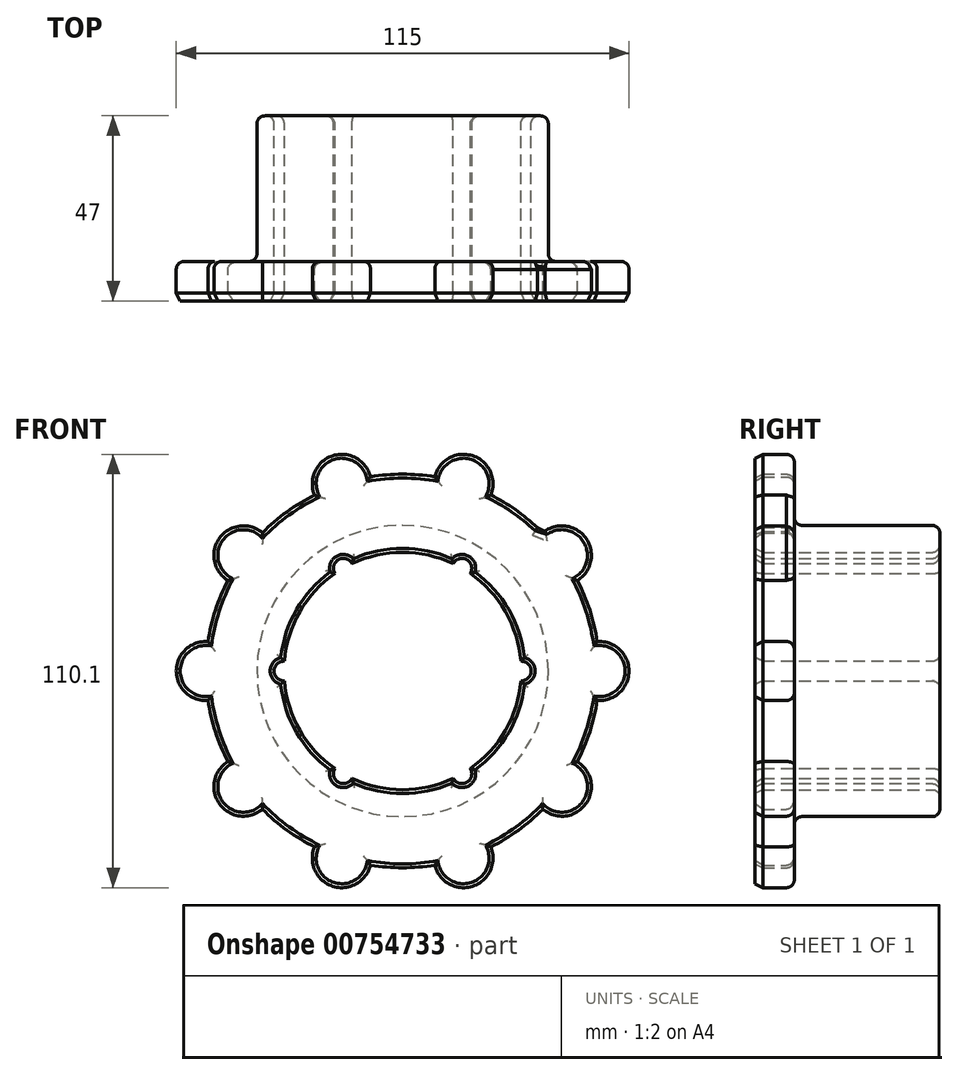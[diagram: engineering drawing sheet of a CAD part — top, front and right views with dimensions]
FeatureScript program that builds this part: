
annotation { "Feature Type Name" : "Feature", "Feature Type Description" : "" }
export const myFeature = defineFeature(function(context is Context, id is Id, definition is map)
    precondition{}
    {
        {
            var Q0;
            Q0=qCreatedBy(makeId("Front.planeOp"),FACE);
            var sketch = newSketch(context, id + "F0", { "sketchPlane" : qUnion([Q0])});
            skArc(sketch, "E0", {"start": v(30.05, 2.5) * mm, "mid": v(26.11, 15.07) * mm, "end": v(17.19, 24.77) * mm});
            skArc(sketch, "E1", {"start": v(30.05, -2.5) * mm, "mid": v(32.65, 0) * mm, "end": v(30.05, 2.5) * mm});
            skArc(sketch, "E2.1.0", {"start": v(17.19, 24.77) * mm, "mid": v(16.33, 28.28) * mm, "end": v(12.86, 27.27) * mm});
            skArc(sketch, "E2.2.0", {"start": v(-12.86, 27.27) * mm, "mid": v(-16.32, 28.28) * mm, "end": v(-17.19, 24.77) * mm});
            skArc(sketch, "E2.3.0", {"start": v(-30.05, 2.5) * mm, "mid": v(-32.65, 0) * mm, "end": v(-30.05, -2.5) * mm});
            skArc(sketch, "E2.4.0", {"start": v(-17.19, -24.77) * mm, "mid": v(-16.33, -28.28) * mm, "end": v(-12.86, -27.27) * mm});
            skArc(sketch, "E2.5.0", {"start": v(12.86, -27.27) * mm, "mid": v(16.33, -28.28) * mm, "end": v(17.19, -24.77) * mm});
            skArc(sketch, "E3.trimOffspring", {"start": v(-17.19, 24.77) * mm, "mid": v(-26.11, 15.08) * mm, "end": v(-30.05, 2.5) * mm});
            skArc(sketch, "E4.trimOffspring", {"start": v(-30.05, -2.5) * mm, "mid": v(-26.11, -15.07) * mm, "end": v(-17.19, -24.77) * mm});
            skArc(sketch, "E5.trimOffspring", {"start": v(-12.86, -27.27) * mm, "mid": v(0, -30.15) * mm, "end": v(12.86, -27.27) * mm});
            skArc(sketch, "E6.trimOffspring", {"start": v(17.19, -24.77) * mm, "mid": v(26.11, -15.07) * mm, "end": v(30.05, -2.5) * mm});
            skArc(sketch, "E7.trimOffspring", {"start": v(12.86, 27.27) * mm, "mid": v(0, 30.15) * mm, "end": v(-12.86, 27.27) * mm});
            skCircle(sketch, "E8", {"center": v(0, 0) * mm, "radius": 37 * mm});
            skSolve(sketch);
        }
        {
            var Q0;
            Q0=makeQuery(id+"F0.imprint","IMPRINT",FACE,{"disambiguationData":[TD([[makeQuery(id+"F0.imprint","IMPRINT",EDGE,{"derivedFrom":sQuery(id+"F0.wireOp",EDGE,"E0")}),-1.0]])]});
            extrude(context, id + "F1", {"entities" : qUnion([Q0]), "depth" : (24 + 13) * mm, "offsetDistance" : 25 * mm});
        }
        {
            var Q0;
            Q0=makeQuery(id+"F1.opExtrude","CAP_FACE",FACE,{"disambiguationData":[OSD([sQuery(id+"F0.wireOp",EDGE,"E0"),sQuery(id+"F0.wireOp",EDGE,"E1"),sQuery(id+"F0.wireOp",EDGE,"E2.1.0"),sQuery(id+"F0.wireOp",EDGE,"E2.2.0"),sQuery(id+"F0.wireOp",EDGE,"E2.3.0"),sQuery(id+"F0.wireOp",EDGE,"E2.4.0"),sQuery(id+"F0.wireOp",EDGE,"E2.5.0"),sQuery(id+"F0.wireOp",EDGE,"E3.trimOffspring"),sQuery(id+"F0.wireOp",EDGE,"E4.trimOffspring"),sQuery(id+"F0.wireOp",EDGE,"E5.trimOffspring"),sQuery(id+"F0.wireOp",EDGE,"E6.trimOffspring"),sQuery(id+"F0.wireOp",EDGE,"E7.trimOffspring"),sQuery(id+"F0.wireOp",EDGE,"E8")])],"isStart":false});
            var sketch = newSketch(context, id + "F2", { "sketchPlane" : qUnion([Q0])});
            skArc(sketch, "E9", {"start": v(-49.44, -7.48) * mm, "mid": v(-47.55, -15.45) * mm, "end": v(-44.4, -23) * mm});
            skArc(sketch, "E10", {"start": v(-49.44, 7.48) * mm, "mid": v(-57.5, 0) * mm, "end": v(-49.44, -7.48) * mm});
            skArc(sketch, "E11.1.0", {"start": v(-44.4, -23) * mm, "mid": v(-46.52, -33.8) * mm, "end": v(-35.6, -35.1) * mm});
            skArc(sketch, "E11.2.0", {"start": v(-22.39, -44.7) * mm, "mid": v(-17.77, -54.69) * mm, "end": v(-8.16, -49.33) * mm});
            skArc(sketch, "E11.3.0", {"start": v(8.16, -49.33) * mm, "mid": v(17.77, -54.69) * mm, "end": v(22.39, -44.7) * mm});
            skArc(sketch, "E11.4.0", {"start": v(35.6, -35.1) * mm, "mid": v(46.52, -33.8) * mm, "end": v(44.4, -23) * mm});
            skArc(sketch, "E11.5.0", {"start": v(49.44, -7.48) * mm, "mid": v(57.5, 0) * mm, "end": v(49.44, 7.48) * mm});
            skArc(sketch, "E11.6.0", {"start": v(44.4, 23) * mm, "mid": v(46.52, 33.8) * mm, "end": v(35.6, 35.1) * mm});
            skArc(sketch, "E11.7.0", {"start": v(22.39, 44.7) * mm, "mid": v(17.77, 54.69) * mm, "end": v(8.16, 49.33) * mm});
            skArc(sketch, "E11.8.0", {"start": v(-8.16, 49.33) * mm, "mid": v(-17.77, 54.69) * mm, "end": v(-22.39, 44.7) * mm});
            skArc(sketch, "E11.9.0", {"start": v(-35.6, 35.1) * mm, "mid": v(-46.52, 33.8) * mm, "end": v(-44.4, 23) * mm});
            skArc(sketch, "E12.trimOffspring", {"start": v(-44.4, 23) * mm, "mid": v(-47.55, 15.45) * mm, "end": v(-49.44, 7.48) * mm});
            skArc(sketch, "E13.trimOffspring", {"start": v(-22.39, 44.7) * mm, "mid": v(-29.39, 40.45) * mm, "end": v(-35.6, 35.1) * mm});
            skArc(sketch, "E14.trimOffspring", {"start": v(8.16, 49.33) * mm, "mid": v(0, 50) * mm, "end": v(-8.16, 49.33) * mm});
            skArc(sketch, "E15.trimOffspring", {"start": v(35.6, 35.1) * mm, "mid": v(29.39, 40.45) * mm, "end": v(22.39, 44.7) * mm});
            skArc(sketch, "E16.trimOffspring", {"start": v(49.44, 7.48) * mm, "mid": v(47.55, 15.45) * mm, "end": v(44.4, 23) * mm});
            skArc(sketch, "E17.trimOffspring", {"start": v(44.4, -23) * mm, "mid": v(47.55, -15.45) * mm, "end": v(49.44, -7.48) * mm});
            skArc(sketch, "E18.trimOffspring", {"start": v(22.39, -44.7) * mm, "mid": v(29.39, -40.45) * mm, "end": v(35.6, -35.1) * mm});
            skArc(sketch, "E19.trimOffspring", {"start": v(-8.16, -49.33) * mm, "mid": v(0, -50) * mm, "end": v(8.16, -49.33) * mm});
            skArc(sketch, "E20.trimOffspring", {"start": v(-35.6, -35.1) * mm, "mid": v(-29.39, -40.45) * mm, "end": v(-22.39, -44.7) * mm});
            skSolve(sketch);
        }
        {
            var Q0;
            Q0=makeQuery(id+"F2.imprint","IMPRINT",FACE,{"disambiguationData":[TD([[makeQuery(id+"F2.imprint","IMPRINT",EDGE,{"derivedFrom":sQuery(id+"F2.wireOp",EDGE,"E9")}),1.0]])]});
            var Q1;
            Q1=makeQuery(id+"F2.imprint","IMPRINT",FACE,{"disambiguationData":[TD([[makeQuery(id+"F2.imprint","IMPRINT",EDGE,{"derivedFrom":makeQuery(id+"F1.opExtrude","CAP_EDGE",EDGE,{"disambiguationData":[OSD([sQuery(id+"F0.wireOp",EDGE,"E0")])],"isStart":false})}),-1.0]])]});
            var Q2;
            Q2=makeQuery(id+"F1.opExtrude","CAP_FACE",FACE,{"disambiguationData":[OSD([sQuery(id+"F0.wireOp",EDGE,"E0"),sQuery(id+"F0.wireOp",EDGE,"E1"),sQuery(id+"F0.wireOp",EDGE,"E2.1.0"),sQuery(id+"F0.wireOp",EDGE,"E2.2.0"),sQuery(id+"F0.wireOp",EDGE,"E2.3.0"),sQuery(id+"F0.wireOp",EDGE,"E2.4.0"),sQuery(id+"F0.wireOp",EDGE,"E2.5.0"),sQuery(id+"F0.wireOp",EDGE,"E3.trimOffspring"),sQuery(id+"F0.wireOp",EDGE,"E4.trimOffspring"),sQuery(id+"F0.wireOp",EDGE,"E5.trimOffspring"),sQuery(id+"F0.wireOp",EDGE,"E6.trimOffspring"),sQuery(id+"F0.wireOp",EDGE,"E7.trimOffspring"),sQuery(id+"F0.wireOp",EDGE,"E8")])],"isStart":false});
            var Q3;
            Q3=makeQuery(id+"F1.opExtrude","CAP_FACE",FACE,{"disambiguationData":[OSD([sQuery(id+"F0.wireOp",EDGE,"E0"),sQuery(id+"F0.wireOp",EDGE,"E1"),sQuery(id+"F0.wireOp",EDGE,"E2.1.0"),sQuery(id+"F0.wireOp",EDGE,"E2.2.0"),sQuery(id+"F0.wireOp",EDGE,"E2.3.0"),sQuery(id+"F0.wireOp",EDGE,"E2.4.0"),sQuery(id+"F0.wireOp",EDGE,"E2.5.0"),sQuery(id+"F0.wireOp",EDGE,"E3.trimOffspring"),sQuery(id+"F0.wireOp",EDGE,"E4.trimOffspring"),sQuery(id+"F0.wireOp",EDGE,"E5.trimOffspring"),sQuery(id+"F0.wireOp",EDGE,"E6.trimOffspring"),sQuery(id+"F0.wireOp",EDGE,"E7.trimOffspring"),sQuery(id+"F0.wireOp",EDGE,"E8")])],"isStart":true});
            extrude(context, id + "F3", {"entities" : qUnion([Q0, Q1, Q2, Q3]), "operationType" : NewBodyOperationType.ADD, "depth" : 10 * mm, "offsetDistance" : 25 * mm});
        }
        {
            var Q0;
            {var subQ0=sQuery(id+"F0.wireOp",EDGE,"E7.trimOffspring");var subQ1=sQuery(id+"F0.wireOp",EDGE,"E6.trimOffspring");var subQ2=sQuery(id+"F0.wireOp",EDGE,"E5.trimOffspring");var subQ3=sQuery(id+"F0.wireOp",EDGE,"E4.trimOffspring");var subQ4=sQuery(id+"F0.wireOp",EDGE,"E3.trimOffspring");var subQ5=sQuery(id+"F0.wireOp",EDGE,"E2.5.0");var subQ6=sQuery(id+"F0.wireOp",EDGE,"E2.4.0");var subQ7=sQuery(id+"F0.wireOp",EDGE,"E2.3.0");var subQ8=sQuery(id+"F0.wireOp",EDGE,"E2.2.0");var subQ9=sQuery(id+"F0.wireOp",EDGE,"E2.1.0");var subQ10=sQuery(id+"F0.wireOp",EDGE,"E1");var subQ11=sQuery(id+"F0.wireOp",EDGE,"E0");var subQ12=sQuery(id+"F0.wireOp",EDGE,"E8");Q0=makeQuery(id+"F3.boolean.opBoolean","MERGE",FACE,{"derivedFrom":[makeQuery(id+"F3.opExtrude","CAP_FACE",FACE,{"disambiguationData":[OSD([subQ11,subQ10,subQ9,subQ8,subQ7,subQ6,subQ5,subQ4,subQ3,subQ2,subQ1,subQ0,subQ12]),TDD([makeQuery(id+"F1.opExtrude","CAP_FACE",FACE,{"disambiguationData":[OSD([subQ11,subQ10,subQ9,subQ8,subQ7,subQ6,subQ5,subQ4,subQ3,subQ2,subQ1,subQ0,subQ12])],"isStart":false})])],"isStart":false}),makeQuery(id+"F3.opExtrude","CAP_FACE",FACE,{"disambiguationData":[OSD([subQ11,subQ10,subQ9,subQ8,subQ7,subQ6,subQ5,subQ4,subQ3,subQ2,subQ1,subQ0,sQuery(id+"F2.wireOp",EDGE,"E9"),sQuery(id+"F2.wireOp",EDGE,"E10"),sQuery(id+"F2.wireOp",EDGE,"E11.1.0"),sQuery(id+"F2.wireOp",EDGE,"E11.2.0"),sQuery(id+"F2.wireOp",EDGE,"E11.3.0"),sQuery(id+"F2.wireOp",EDGE,"E11.4.0"),sQuery(id+"F2.wireOp",EDGE,"E11.5.0"),sQuery(id+"F2.wireOp",EDGE,"E11.6.0"),sQuery(id+"F2.wireOp",EDGE,"E11.7.0"),sQuery(id+"F2.wireOp",EDGE,"E11.8.0"),sQuery(id+"F2.wireOp",EDGE,"E11.9.0"),sQuery(id+"F2.wireOp",EDGE,"E12.trimOffspring"),sQuery(id+"F2.wireOp",EDGE,"E13.trimOffspring"),sQuery(id+"F2.wireOp",EDGE,"E14.trimOffspring"),sQuery(id+"F2.wireOp",EDGE,"E15.trimOffspring"),sQuery(id+"F2.wireOp",EDGE,"E16.trimOffspring"),sQuery(id+"F2.wireOp",EDGE,"E17.trimOffspring"),sQuery(id+"F2.wireOp",EDGE,"E18.trimOffspring"),sQuery(id+"F2.wireOp",EDGE,"E19.trimOffspring"),sQuery(id+"F2.wireOp",EDGE,"E20.trimOffspring")])],"isStart":false})]});}
            var Q1;
            Q1=makeQuery(id+"F3.opExtrude","SWEPT_EDGE",EDGE,{"disambiguationData":[OSD([sQuery(id+"F2.wireOp",EDGE,"E11.6.0"),sQuery(id+"F2.wireOp",EDGE,"E15.trimOffspring")])]});
            var Q2;
            Q2=makeQuery(id+"F3.opExtrude","CAP_EDGE",EDGE,{"disambiguationData":[OSD([sQuery(id+"F2.wireOp",EDGE,"E15.trimOffspring")])],"isStart":true});
            chamfer(context, id + "F4", {"entities" : qUnion([Q0, Q1, Q2]), "chamferType" : ChamferType.TWO_OFFSETS, "width1" : 2 * mm, "oppositeDirection" : false, "width2" : 1 * mm, "tangentPropagation" : true});
        }
        {
            var Q0;
            {var subQ0=sQuery(id+"F0.wireOp",EDGE,"E7.trimOffspring");var subQ1=sQuery(id+"F0.wireOp",EDGE,"E6.trimOffspring");var subQ2=sQuery(id+"F0.wireOp",EDGE,"E5.trimOffspring");var subQ3=sQuery(id+"F0.wireOp",EDGE,"E4.trimOffspring");var subQ4=sQuery(id+"F0.wireOp",EDGE,"E3.trimOffspring");var subQ5=sQuery(id+"F0.wireOp",EDGE,"E2.5.0");var subQ6=sQuery(id+"F0.wireOp",EDGE,"E2.4.0");var subQ7=sQuery(id+"F0.wireOp",EDGE,"E2.3.0");var subQ8=sQuery(id+"F0.wireOp",EDGE,"E2.2.0");var subQ9=sQuery(id+"F0.wireOp",EDGE,"E2.1.0");var subQ10=sQuery(id+"F0.wireOp",EDGE,"E1");var subQ11=sQuery(id+"F0.wireOp",EDGE,"E0");var subQ12=sQuery(id+"F0.wireOp",EDGE,"E8");Q0=makeQuery(id+"F3.boolean.opBoolean","MERGE",FACE,{"derivedFrom":[makeQuery(id+"F3.opExtrude","CAP_FACE",FACE,{"disambiguationData":[OSD([subQ11,subQ10,subQ9,subQ8,subQ7,subQ6,subQ5,subQ4,subQ3,subQ2,subQ1,subQ0,subQ12]),TDD([makeQuery(id+"F1.opExtrude","CAP_FACE",FACE,{"disambiguationData":[OSD([subQ11,subQ10,subQ9,subQ8,subQ7,subQ6,subQ5,subQ4,subQ3,subQ2,subQ1,subQ0,subQ12])],"isStart":false})])],"isStart":true}),makeQuery(id+"F3.opExtrude","CAP_FACE",FACE,{"disambiguationData":[OSD([subQ11,subQ10,subQ9,subQ8,subQ7,subQ6,subQ5,subQ4,subQ3,subQ2,subQ1,subQ0,sQuery(id+"F2.wireOp",EDGE,"E9"),sQuery(id+"F2.wireOp",EDGE,"E10"),sQuery(id+"F2.wireOp",EDGE,"E11.1.0"),sQuery(id+"F2.wireOp",EDGE,"E11.2.0"),sQuery(id+"F2.wireOp",EDGE,"E11.3.0"),sQuery(id+"F2.wireOp",EDGE,"E11.4.0"),sQuery(id+"F2.wireOp",EDGE,"E11.5.0"),sQuery(id+"F2.wireOp",EDGE,"E11.6.0"),sQuery(id+"F2.wireOp",EDGE,"E11.7.0"),sQuery(id+"F2.wireOp",EDGE,"E11.8.0"),sQuery(id+"F2.wireOp",EDGE,"E11.9.0"),sQuery(id+"F2.wireOp",EDGE,"E12.trimOffspring"),sQuery(id+"F2.wireOp",EDGE,"E13.trimOffspring"),sQuery(id+"F2.wireOp",EDGE,"E14.trimOffspring"),sQuery(id+"F2.wireOp",EDGE,"E15.trimOffspring"),sQuery(id+"F2.wireOp",EDGE,"E16.trimOffspring"),sQuery(id+"F2.wireOp",EDGE,"E17.trimOffspring"),sQuery(id+"F2.wireOp",EDGE,"E18.trimOffspring"),sQuery(id+"F2.wireOp",EDGE,"E19.trimOffspring"),sQuery(id+"F2.wireOp",EDGE,"E20.trimOffspring")])],"isStart":true})]});}
            fillet(context, id + "F5", {"entities" : qUnion([Q0]), "radius" : 2 * mm, "tangentPropagation" : true, "allowEdgeOverflow" : false});
        }
        {
            var Q0;
            Q0=makeQuery(id+"F1.opExtrude","CAP_FACE",FACE,{"disambiguationData":[OSD([sQuery(id+"F0.wireOp",EDGE,"E0"),sQuery(id+"F0.wireOp",EDGE,"E1"),sQuery(id+"F0.wireOp",EDGE,"E2.1.0"),sQuery(id+"F0.wireOp",EDGE,"E2.2.0"),sQuery(id+"F0.wireOp",EDGE,"E2.3.0"),sQuery(id+"F0.wireOp",EDGE,"E2.4.0"),sQuery(id+"F0.wireOp",EDGE,"E2.5.0"),sQuery(id+"F0.wireOp",EDGE,"E3.trimOffspring"),sQuery(id+"F0.wireOp",EDGE,"E4.trimOffspring"),sQuery(id+"F0.wireOp",EDGE,"E5.trimOffspring"),sQuery(id+"F0.wireOp",EDGE,"E6.trimOffspring"),sQuery(id+"F0.wireOp",EDGE,"E7.trimOffspring"),sQuery(id+"F0.wireOp",EDGE,"E8")])],"isStart":true});
            fillet(context, id + "F6", {"entities" : qUnion([Q0]), "radius" : 2 * mm, "tangentPropagation" : true, "allowEdgeOverflow" : false});
        }
    });
